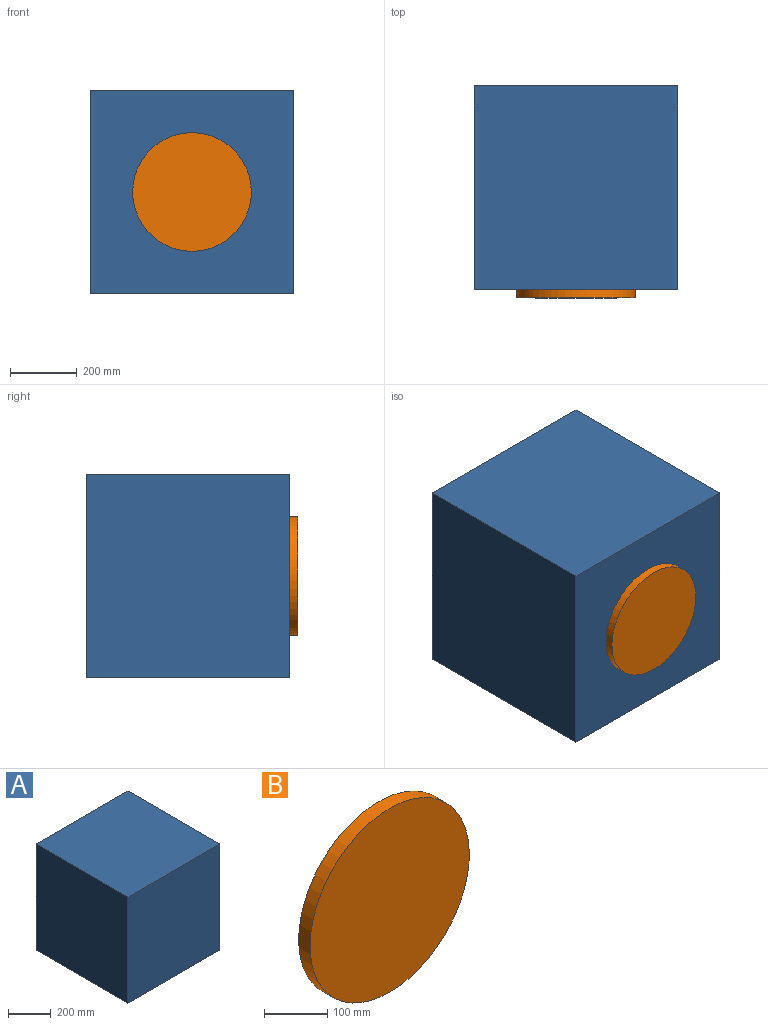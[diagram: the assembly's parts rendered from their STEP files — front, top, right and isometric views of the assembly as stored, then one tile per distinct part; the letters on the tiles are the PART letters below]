
ASSEMBLY  parts=2 mates=1
PART A: 6 faces, bbox 609.6x609.6x609.6 mm
  f0: plane 609.6x609.6mm, normal (0,0,1), area 371612.2mm2, adj f1,f3,f4,f5
  f1: plane 609.6x609.6mm, normal (-1,0,0), area 371612.2mm2, adj f0,f2,f4,f5
  f2: plane 609.6x609.6mm, normal (0,0,-1), area 371612.2mm2, adj f1,f3,f4,f5
  f3: plane 609.6x609.6mm, normal (1,0,0), area 371612.2mm2, adj f0,f2,f4,f5
  f4: plane 609.6x609.6mm, normal (0,-1,0), area 371612.2mm2, adj f0,f1,f2,f3
  f5: plane 609.6x609.6mm, normal (0,1,0), area 371612.2mm2, adj f0,f1,f2,f3
PART B: 3 faces, bbox 355.6x25.4x355.6 mm
  f0: cylinder r=177.8mm len=355.6mm, axis (0,1,0), area 28375.6mm2, adj f1,f2
  f1: plane 355.6x355.6mm, normal (0,-1,0), area 99314.7mm2, adj f0
  f2: plane 355.6x355.6mm, normal (0,1,0), area 99314.7mm2, adj f0
PLACE A at identity
PLACE B t=(0,-304.8,0)mm
MATE fastened B.f0 <-> A.f4  axis (0,1,0) through (0,-304.8,0)mm
